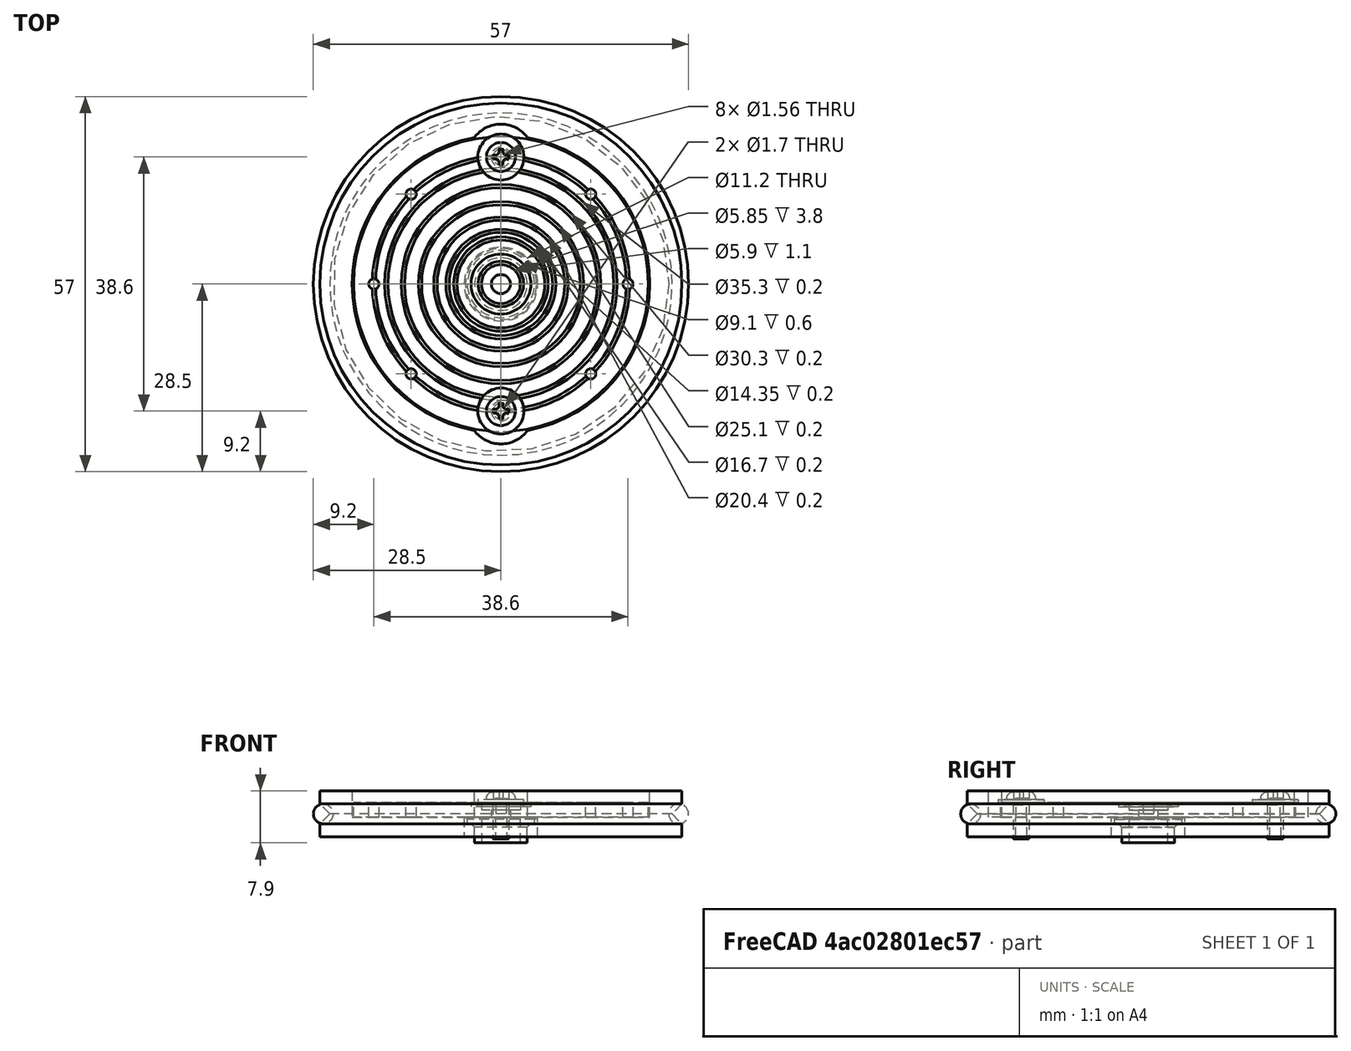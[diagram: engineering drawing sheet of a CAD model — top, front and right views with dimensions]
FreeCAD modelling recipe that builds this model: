
FCSTD DOCUMENT  (FreeCAD 0.14R3702 (Git))
Label: Renacuajo-wheel-big-rounded-horn-assembly
License: CC-BY 3.0
LicenseURL: http://creativecommons.org/licenses/by/3.0/
objects: Part::Feature×4, Part::Torus×1, Part::Compound×1
note: 6 computed .brp shape members not serialized (recipe doc carries the construction recipe); baked Part::Feature solids carry a one-line shape summary decoded from their .brp

FEATURE [Part::Feature] Pocket  label="Renacuajo-wheel-big-rounded-horn-final"
  Placement = pos=(0,0,0) rot=(1,0,0;1.5708rad)
  shape: bbox 55 x 55 x 7 mm, 15 faces (baked)
FEATURE [Part::Feature] Fillet  label="rounded-horn-final001"
  Placement = pos=(0,0,-0.5) rot=(0,0,1;0rad)
  shape: bbox 44.8 x 44.8 x 6.1 mm, 76 faces (baked)
FEATURE [Part::Feature] Chamfer  label="screw1"
  Placement = pos=(0,-19.3,1.7) rot=(0,0,1;0rad)
  shape: bbox 7 x 7 x 7.14 mm, 33 faces (baked)
FEATURE [Part::Feature] Chamfer001  label="screw002"
  Placement = pos=(0,19.3,1.7) rot=(0,0,1;0rad)
  shape: bbox 7 x 7 x 7.14 mm, 33 faces (baked)
FEATURE [Part::Torus] Torus  label="o-ring"
  Angle1 = -180
  Angle2 = 180
  Angle3 = 360
  Radius1 = 27
  Radius2 = 1.5
FEATURE [Part::Compound] Compound  label="Renacuajo-wheel-big-rounded-horn-assembly-final"
  Links = -> [Pocket,Chamfer001,Fillet,Chamfer,Torus]
